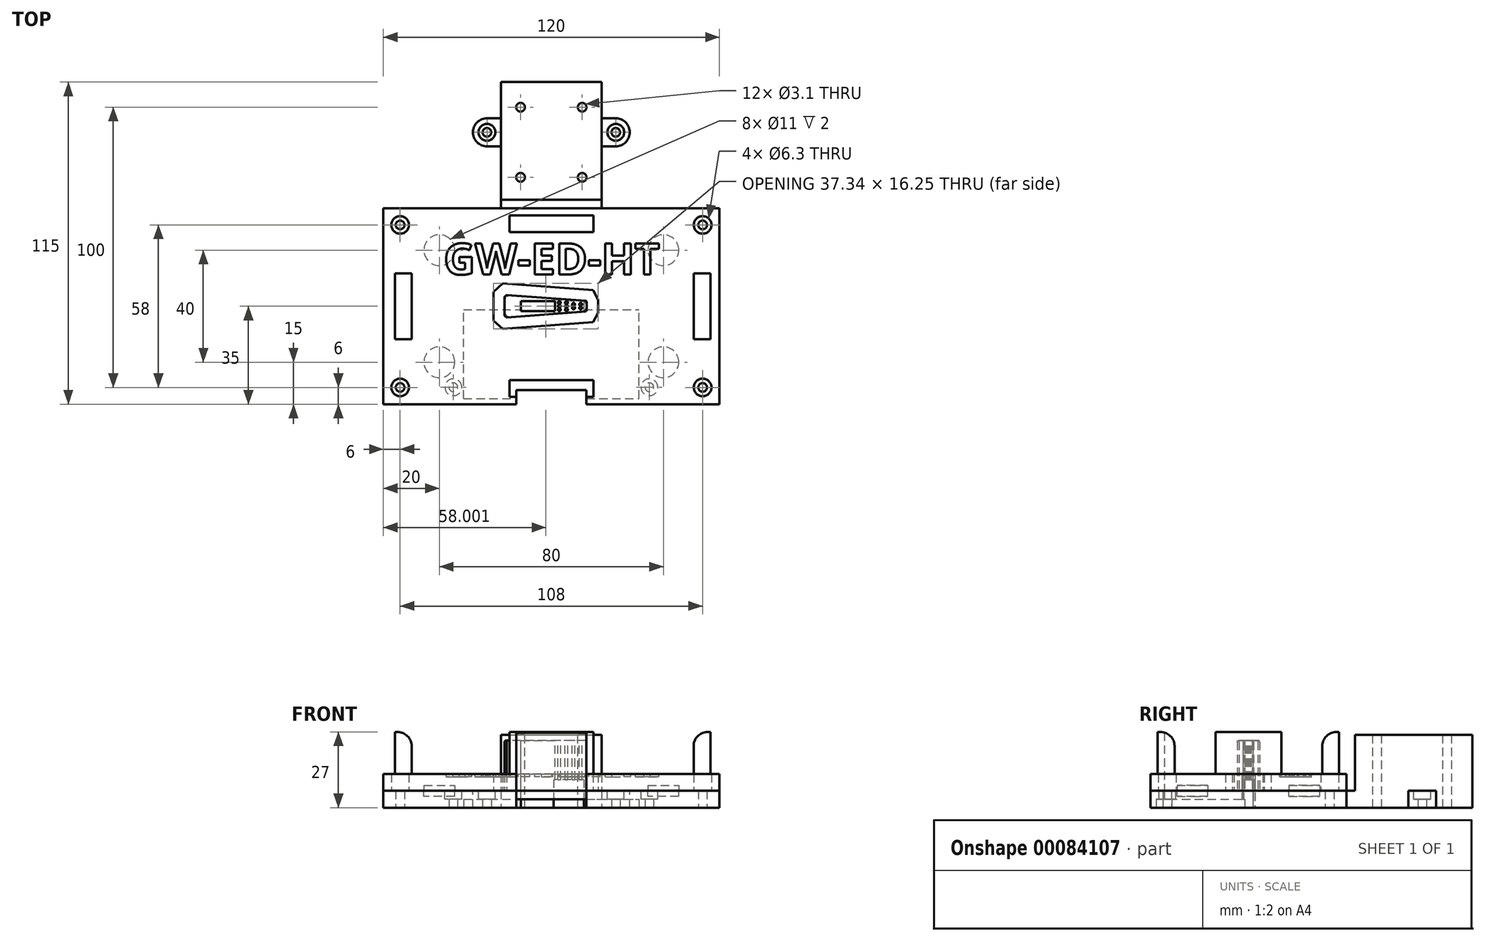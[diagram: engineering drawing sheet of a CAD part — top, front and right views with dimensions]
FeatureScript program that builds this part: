
annotation { "Feature Type Name" : "Feature", "Feature Type Description" : "" }
export const myFeature = defineFeature(function(context is Context, id is Id, definition is map)
    precondition{}
    {
        {
            var Q0;
            Q0=qCreatedBy(makeId("Top.planeOp"),FACE);
            var sketch = newSketch(context, id + "F0", { "sketchPlane" : qUnion([Q0])});
            skLineSegment(sketch, "E0.bottom", {"start": v(-60, 35) * mm, "end": v(60, 35) * mm});
            skLineSegment(sketch, "E0.top", {"start": v(-60, -35) * mm, "end": v(60, -35) * mm});
            skLineSegment(sketch, "E0.left", {"start": v(-60, 35) * mm, "end": v(-60, -35) * mm});
            skLineSegment(sketch, "E0.right", {"start": v(60, 35) * mm, "end": v(60, -35) * mm});
            skCircle(sketch, "E1", {"center": v(-54, 29) * mm, "radius": 1.55 * mm});
            skCircle(sketch, "E2", {"center": v(54, 29) * mm, "radius": 1.55 * mm});
            skCircle(sketch, "E3", {"center": v(54, -29) * mm, "radius": 1.55 * mm});
            skCircle(sketch, "E4", {"center": v(-54, -29) * mm, "radius": 1.55 * mm});
            skLineSegment(sketch, "E5.bottom", {"start": v(-18, 35) * mm, "end": v(18, 35) * mm});
            skLineSegment(sketch, "E5.top", {"start": v(-18, 80) * mm, "end": v(18, 80) * mm});
            skLineSegment(sketch, "E5.left", {"start": v(-18, 35) * mm, "end": v(-18, 80) * mm});
            skLineSegment(sketch, "E5.right", {"start": v(18, 35) * mm, "end": v(18, 80) * mm});
            skLineSegment(sketch, "E6.bottom", {"start": v(-18, 67.06) * mm, "end": v(-28, 67.06) * mm});
            skLineSegment(sketch, "E6.top", {"start": v(-18, 57.06) * mm, "end": v(-28, 57.06) * mm});
            skLineSegment(sketch, "E6.left", {"start": v(-18, 67.06) * mm, "end": v(-18, 57.06) * mm});
            skLineSegment(sketch, "E6.right", {"start": v(-28, 67.06) * mm, "end": v(-28, 57.06) * mm});
            skLineSegment(sketch, "E7.bottom", {"start": v(18, 67.06) * mm, "end": v(28, 67.06) * mm});
            skLineSegment(sketch, "E7.top", {"start": v(18, 57.06) * mm, "end": v(28, 57.06) * mm});
            skLineSegment(sketch, "E7.left", {"start": v(18, 67.06) * mm, "end": v(18, 57.06) * mm});
            skLineSegment(sketch, "E7.right", {"start": v(28, 67.06) * mm, "end": v(28, 57.06) * mm});
            skCircle(sketch, "E8", {"center": v(-23, 62.06) * mm, "radius": 1.55 * mm});
            skCircle(sketch, "E9", {"center": v(23, 62.06) * mm, "radius": 1.55 * mm});
            skCircle(sketch, "E10", {"center": v(-35, -28.94) * mm, "radius": 1.55 * mm});
            skCircle(sketch, "E11", {"center": v(35, -28.94) * mm, "radius": 1.55 * mm});
            skPoint(sketch, "E12", {"position": v(-28, 62.06) * mm});
            skSolve(sketch);
        }
        {
            var Q0;
            Q0 = qSketchRegion(id + "F0", true);
            extrude(context, id + "F1", {"entities" : qUnion([Q0]), "depth" : 6 * mm});
        }
        {
            var Q0;
            Q0=makeQuery(id+"F1.opExtrude","CAP_FACE",FACE,{"disambiguationData":[OSD([sQuery(id+"F0.wireOp",EDGE,"E0.bottom"),sQuery(id+"F0.wireOp",EDGE,"E0.top"),sQuery(id+"F0.wireOp",EDGE,"E0.left"),sQuery(id+"F0.wireOp",EDGE,"E0.right"),sQuery(id+"F0.wireOp",EDGE,"E1"),sQuery(id+"F0.wireOp",EDGE,"E2"),sQuery(id+"F0.wireOp",EDGE,"E3"),sQuery(id+"F0.wireOp",EDGE,"E4")])],"isStart":false});
            var sketch = newSketch(context, id + "F2", { "sketchPlane" : qUnion([Q0])});
            skLineSegment(sketch, "E13.0", {"start": v(12.67, -1.36) * mm, "end": v(12.67, 1.36) * mm});
            skLineSegment(sketch, "E13.1", {"start": v(12.4, -1.88) * mm, "end": v(12.67, -1.36) * mm});
            skLineSegment(sketch, "E13.2", {"start": v(12.67, 1.36) * mm, "end": v(12.4, 1.88) * mm});
            skLineSegment(sketch, "E13.3", {"start": v(-15.98, -4) * mm, "end": v(12.4, -1.88) * mm});
            skLineSegment(sketch, "E13.4", {"start": v(12.4, 1.88) * mm, "end": v(-15.98, 4) * mm});
            skLineSegment(sketch, "E13.5", {"start": v(-15.98, 4) * mm, "end": v(-16.67, 3.38) * mm});
            skLineSegment(sketch, "E13.6", {"start": v(-16.67, 3.38) * mm, "end": v(-16.67, -3.38) * mm});
            skLineSegment(sketch, "E13.7", {"start": v(-16.67, -3.38) * mm, "end": v(-15.98, -4) * mm});
            skSolve(sketch);
        }
        {
            var Q0;
            Q0 = qSketchRegion(id + "F2", true);
            extrude(context, id + "F3", {"entities" : qUnion([Q0]), "operationType" : NewBodyOperationType.ADD, "depth" : 18 * mm});
        }
        {
            var Q0;
            Q0=makeQuery(id+"F3.opExtrude","CAP_FACE",FACE,{"disambiguationData":[OSD([sQuery(id+"F2.wireOp",EDGE,"E13.0"),sQuery(id+"F2.wireOp",EDGE,"E13.1"),sQuery(id+"F2.wireOp",EDGE,"E13.2"),sQuery(id+"F2.wireOp",EDGE,"E13.3"),sQuery(id+"F2.wireOp",EDGE,"E13.4"),sQuery(id+"F2.wireOp",EDGE,"E13.5"),sQuery(id+"F2.wireOp",EDGE,"E13.6"),sQuery(id+"F2.wireOp",EDGE,"E13.7")])],"isStart":false});
            var sketch = newSketch(context, id + "F4", { "sketchPlane" : qUnion([Q0])});
            skCircle(sketch, "E14", {"center": v(10.47, 0.64) * mm, "radius": 0.5 * mm});
            skCircle(sketch, "E15", {"center": v(10.47, -0.64) * mm, "radius": 0.5 * mm});
            skCircle(sketch, "E16", {"center": v(7.93, 0.64) * mm, "radius": 0.5 * mm});
            skCircle(sketch, "E17", {"center": v(7.93, -0.64) * mm, "radius": 0.5 * mm});
            skCircle(sketch, "E18", {"center": v(5.4, 1.27) * mm, "radius": 0.5 * mm});
            skCircle(sketch, "E19", {"center": v(5.4, 0) * mm, "radius": 0.5 * mm});
            skCircle(sketch, "E20", {"center": v(5.4, -1.27) * mm, "radius": 0.5 * mm});
            skCircle(sketch, "E21", {"center": v(2.85, 1.27) * mm, "radius": 0.5 * mm});
            skCircle(sketch, "E22", {"center": v(2.85, 0) * mm, "radius": 0.5 * mm});
            skCircle(sketch, "E23", {"center": v(2.85, -1.27) * mm, "radius": 0.5 * mm});
            skLineSegment(sketch, "E24.bottom", {"start": v(-10.87, 1.78) * mm, "end": v(1.35, 1.78) * mm});
            skLineSegment(sketch, "E24.top", {"start": v(-10.87, -1.78) * mm, "end": v(1.35, -1.78) * mm});
            skLineSegment(sketch, "E24.left", {"start": v(-10.87, 1.78) * mm, "end": v(-10.87, -1.78) * mm});
            skLineSegment(sketch, "E24.right", {"start": v(1.35, 1.78) * mm, "end": v(1.35, -1.78) * mm});
            skSolve(sketch);
        }
        {
            var Q0;
            Q0 = qSketchRegion(id + "F4", true);
            extrude(context, id + "F5", {"entities" : qUnion([Q0]), "operationType" : NewBodyOperationType.REMOVE, "endBound" : BoundingType.THROUGH_ALL, "oppositeDirection" : true, "depth" : 25 * mm});
        }
        {
            var Q0;
            Q0=makeQuery(id+"F1.opExtrude","CAP_FACE",FACE,{"disambiguationData":[OSD([sQuery(id+"F0.wireOp",EDGE,"E0.bottom"),sQuery(id+"F0.wireOp",EDGE,"E0.top"),sQuery(id+"F0.wireOp",EDGE,"E0.left"),sQuery(id+"F0.wireOp",EDGE,"E0.right"),sQuery(id+"F0.wireOp",EDGE,"E1"),sQuery(id+"F0.wireOp",EDGE,"E2"),sQuery(id+"F0.wireOp",EDGE,"E3"),sQuery(id+"F0.wireOp",EDGE,"E4")])],"isStart":true});
            var sketch = newSketch(context, id + "F6", { "sketchPlane" : qUnion([Q0])});
            skLineSegment(sketch, "E25", {"start": v(0.79, 2.33) * mm, "end": v(0.79, -2.33) * mm});
            skLineSegment(sketch, "E26", {"start": v(0.79, -2.33) * mm, "end": v(11.64, -1.64) * mm});
            skLineSegment(sketch, "E27", {"start": v(11.64, -1.64) * mm, "end": v(11.64, 1.64) * mm});
            skLineSegment(sketch, "E28", {"start": v(11.64, 1.64) * mm, "end": v(0.79, 2.33) * mm});
            skSolve(sketch);
        }
        {
            var Q0;
            Q0 = qSketchRegion(id + "F6", true);
            extrude(context, id + "F7", {"entities" : qUnion([Q0]), "operationType" : NewBodyOperationType.REMOVE, "oppositeDirection" : true, "depth" : 10 * mm});
        }
        {
            var Q0;
            Q0=makeQuery(id+"F1.opExtrude","CAP_FACE",FACE,{"disambiguationData":[OSD([sQuery(id+"F0.wireOp",EDGE,"E0.bottom"),sQuery(id+"F0.wireOp",EDGE,"E0.top"),sQuery(id+"F0.wireOp",EDGE,"E0.left"),sQuery(id+"F0.wireOp",EDGE,"E0.right"),sQuery(id+"F0.wireOp",EDGE,"E1"),sQuery(id+"F0.wireOp",EDGE,"E2"),sQuery(id+"F0.wireOp",EDGE,"E3"),sQuery(id+"F0.wireOp",EDGE,"E4")])],"isStart":false});
            var sketch = newSketch(context, id + "F8", { "sketchPlane" : qUnion([Q0])});
            skLineSegment(sketch, "E29.bottom", {"start": v(-60, 35) * mm, "end": v(60, 35) * mm});
            skLineSegment(sketch, "E29.top", {"start": v(-60, -35) * mm, "end": v(60, -35) * mm});
            skLineSegment(sketch, "E29.left", {"start": v(-60, 35) * mm, "end": v(-60, -35) * mm});
            skLineSegment(sketch, "E29.right", {"start": v(60, 35) * mm, "end": v(60, -35) * mm});
            skCircle(sketch, "E30", {"center": v(-54, 29) * mm, "radius": 3.15 * mm});
            skCircle(sketch, "E31", {"center": v(54, 29) * mm, "radius": 3.15 * mm});
            skCircle(sketch, "E32", {"center": v(54, -29) * mm, "radius": 3.15 * mm});
            skCircle(sketch, "E33", {"center": v(-54, -29) * mm, "radius": 3.15 * mm});
            skLineSegment(sketch, "E34.0", {"start": v(-20.67, -5.14) * mm, "end": v(-17.4, -8.13) * mm});
            skLineSegment(sketch, "E34.1", {"start": v(-20.67, 5.14) * mm, "end": v(-20.67, -5.14) * mm});
            skLineSegment(sketch, "E34.2", {"start": v(-17.4, -8.13) * mm, "end": v(14.9, -5.7) * mm});
            skLineSegment(sketch, "E34.3", {"start": v(-17.4, 8.13) * mm, "end": v(-20.67, 5.14) * mm});
            skLineSegment(sketch, "E34.4", {"start": v(14.9, -5.7) * mm, "end": v(16.67, -2.35) * mm});
            skLineSegment(sketch, "E34.5", {"start": v(16.67, -2.35) * mm, "end": v(16.67, 2.35) * mm});
            skLineSegment(sketch, "E34.6", {"start": v(16.67, 2.35) * mm, "end": v(14.9, 5.7) * mm});
            skLineSegment(sketch, "E34.7", {"start": v(14.9, 5.7) * mm, "end": v(-17.4, 8.13) * mm});
            skSolve(sketch);
        }
        {
            var Q0;
            Q0 = qSketchRegion(id + "F8", true);
            extrude(context, id + "F9", {"entities" : qUnion([Q0]), "depth" : 6 * mm});
        }
        {
            var Q0;
            Q0=makeQuery(id+"F9.opExtrude","CAP_FACE",FACE,{"disambiguationData":[OSD([sQuery(id+"F8.wireOp",EDGE,"E29.bottom"),sQuery(id+"F8.wireOp",EDGE,"E29.top"),sQuery(id+"F8.wireOp",EDGE,"E29.left"),sQuery(id+"F8.wireOp",EDGE,"E29.right"),sQuery(id+"F8.wireOp",EDGE,"E30"),sQuery(id+"F8.wireOp",EDGE,"E31"),sQuery(id+"F8.wireOp",EDGE,"E32"),sQuery(id+"F8.wireOp",EDGE,"E33"),sQuery(id+"F8.wireOp",EDGE,"E34.0"),sQuery(id+"F8.wireOp",EDGE,"E34.1"),sQuery(id+"F8.wireOp",EDGE,"E34.2"),sQuery(id+"F8.wireOp",EDGE,"E34.3"),sQuery(id+"F8.wireOp",EDGE,"E34.4"),sQuery(id+"F8.wireOp",EDGE,"E34.5"),sQuery(id+"F8.wireOp",EDGE,"E34.6"),sQuery(id+"F8.wireOp",EDGE,"E34.7")])],"isStart":false});
            var sketch = newSketch(context, id + "F10", { "sketchPlane" : qUnion([Q0])});
            skLineSegment(sketch, "E35.bottom", {"start": v(-55.9, 11.73) * mm, "end": v(-49.9, 11.73) * mm});
            skLineSegment(sketch, "E35.top", {"start": v(-55.9, -11.73) * mm, "end": v(-49.9, -11.73) * mm});
            skLineSegment(sketch, "E35.left", {"start": v(-55.9, 11.73) * mm, "end": v(-55.9, -11.73) * mm});
            skLineSegment(sketch, "E35.right", {"start": v(-49.9, 11.73) * mm, "end": v(-49.9, -11.73) * mm});
            skLineSegment(sketch, "E36.bottom", {"start": v(-15, 32.38) * mm, "end": v(15, 32.38) * mm});
            skLineSegment(sketch, "E36.top", {"start": v(-15, 26.38) * mm, "end": v(15, 26.37) * mm});
            skLineSegment(sketch, "E36.left", {"start": v(-15, 32.37) * mm, "end": v(-15, 26.37) * mm});
            skLineSegment(sketch, "E36.right", {"start": v(15, 32.37) * mm, "end": v(15, 26.37) * mm});
            skLineSegment(sketch, "E37.bottom", {"start": v(-15, -26.37) * mm, "end": v(15, -26.38) * mm});
            skLineSegment(sketch, "E37.top", {"start": v(-15, -32.37) * mm, "end": v(15, -32.37) * mm});
            skLineSegment(sketch, "E37.left", {"start": v(-15, -26.37) * mm, "end": v(-15, -32.37) * mm});
            skLineSegment(sketch, "E37.right", {"start": v(15, -26.37) * mm, "end": v(15, -32.37) * mm});
            skLineSegment(sketch, "E38.bottom", {"start": v(50.8, 11.73) * mm, "end": v(56.8, 11.73) * mm});
            skLineSegment(sketch, "E38.top", {"start": v(50.8, -11.73) * mm, "end": v(56.8, -11.73) * mm});
            skLineSegment(sketch, "E38.left", {"start": v(50.8, 11.73) * mm, "end": v(50.8, -11.73) * mm});
            skLineSegment(sketch, "E38.right", {"start": v(56.8, 11.73) * mm, "end": v(56.8, -11.73) * mm});
            skSolve(sketch);
        }
        {
            var Q0;
            Q0 = qSketchRegion(id + "F10", true);
            extrude(context, id + "F11", {"entities" : qUnion([Q0]), "operationType" : NewBodyOperationType.ADD, "depth" : 15 * mm});
        }
        {
            var Q0;
            Q0=makeQuery(id+"F11.opExtrude","CAP_EDGE",EDGE,{"disambiguationData":[OSD([sQuery(id+"F10.wireOp",EDGE,"E37.bottom")])],"isStart":false});
            var Q1;
            Q1=makeQuery(id+"F11.opExtrude","CAP_EDGE",EDGE,{"disambiguationData":[OSD([sQuery(id+"F10.wireOp",EDGE,"E35.right")])],"isStart":false});
            var Q2;
            Q2=makeQuery(id+"F11.opExtrude","CAP_EDGE",EDGE,{"disambiguationData":[OSD([sQuery(id+"F10.wireOp",EDGE,"E36.top")])],"isStart":false});
            var Q3;
            Q3=makeQuery(id+"F11.opExtrude","CAP_EDGE",EDGE,{"disambiguationData":[OSD([sQuery(id+"F10.wireOp",EDGE,"E38.left")])],"isStart":false});
            fillet(context, id + "F12", {"entities" : qUnion([Q0, Q1, Q2, Q3]), "radius" : 5 * mm, "tangentPropagation" : true, "allowEdgeOverflow" : false});
        }
        {
            var Q0;
            Q0=makeQuery(id+"F3.opExtrude","CAP_EDGE",EDGE,{"disambiguationData":[OSD([sQuery(id+"F2.wireOp",EDGE,"E13.3")])],"isStart":false});
            var Q1;
            Q1=makeQuery(id+"F3.opExtrude","CAP_EDGE",EDGE,{"disambiguationData":[OSD([sQuery(id+"F2.wireOp",EDGE,"E13.4")])],"isStart":false});
            var Q2;
            Q2=makeQuery(id+"F3.opExtrude","CAP_EDGE",EDGE,{"disambiguationData":[OSD([sQuery(id+"F2.wireOp",EDGE,"E13.0")])],"isStart":false});
            var Q3;
            Q3=makeQuery(id+"F3.opExtrude","CAP_EDGE",EDGE,{"disambiguationData":[OSD([sQuery(id+"F2.wireOp",EDGE,"E13.2")])],"isStart":false});
            var Q4;
            Q4=makeQuery(id+"F3.opExtrude","CAP_EDGE",EDGE,{"disambiguationData":[OSD([sQuery(id+"F2.wireOp",EDGE,"E13.1")])],"isStart":false});
            var Q5;
            Q5=makeQuery(id+"F3.opExtrude","CAP_EDGE",EDGE,{"disambiguationData":[OSD([sQuery(id+"F2.wireOp",EDGE,"E13.7")])],"isStart":false});
            var Q6;
            Q6=makeQuery(id+"F3.opExtrude","CAP_EDGE",EDGE,{"disambiguationData":[OSD([sQuery(id+"F2.wireOp",EDGE,"E13.6")])],"isStart":false});
            var Q7;
            Q7=makeQuery(id+"F3.opExtrude","CAP_EDGE",EDGE,{"disambiguationData":[OSD([sQuery(id+"F2.wireOp",EDGE,"E13.5")])],"isStart":false});
            fillet(context, id + "F13", {"entities" : qUnion([Q0, Q1, Q2, Q3, Q4, Q5, Q6, Q7]), "radius" : 0.5 * mm, "tangentPropagation" : true, "allowEdgeOverflow" : false});
        }
        {
            var Q0;
            Q0=makeQuery(id+"F1.opExtrude","CAP_FACE",FACE,{"disambiguationData":[OSD([sQuery(id+"F0.wireOp",EDGE,"E0.bottom"),sQuery(id+"F0.wireOp",EDGE,"E0.top"),sQuery(id+"F0.wireOp",EDGE,"E0.left"),sQuery(id+"F0.wireOp",EDGE,"E0.right"),sQuery(id+"F0.wireOp",EDGE,"E1"),sQuery(id+"F0.wireOp",EDGE,"E2"),sQuery(id+"F0.wireOp",EDGE,"E3"),sQuery(id+"F0.wireOp",EDGE,"E4")])],"isStart":true});
            var sketch = newSketch(context, id + "F14", { "sketchPlane" : qUnion([Q0])});
            skLineSegment(sketch, "E39.bottom", {"start": v(-12.5, 35) * mm, "end": v(12.5, 35) * mm});
            skLineSegment(sketch, "E39.top", {"start": v(-12.5, 30) * mm, "end": v(12.5, 30) * mm});
            skLineSegment(sketch, "E39.left", {"start": v(-12.5, 35) * mm, "end": v(-12.5, 30) * mm});
            skLineSegment(sketch, "E39.right", {"start": v(12.5, 35) * mm, "end": v(12.5, 30) * mm});
            skSolve(sketch);
        }
        {
            var Q0;
            Q0 = qSketchRegion(id + "F14", true);
            extrude(context, id + "F15", {"entities" : qUnion([Q0]), "operationType" : NewBodyOperationType.REMOVE, "endBound" : BoundingType.THROUGH_ALL, "oppositeDirection" : true, "depth" : 25 * mm});
        }
        {
            var Q0;
            Q0=makeQuery(id+"F1.opExtrude","CAP_FACE",FACE,{"disambiguationData":[OSD([sQuery(id+"F0.wireOp",EDGE,"E0.bottom"),sQuery(id+"F0.wireOp",EDGE,"E0.top"),sQuery(id+"F0.wireOp",EDGE,"E0.left"),sQuery(id+"F0.wireOp",EDGE,"E0.right"),sQuery(id+"F0.wireOp",EDGE,"E1"),sQuery(id+"F0.wireOp",EDGE,"E2"),sQuery(id+"F0.wireOp",EDGE,"E3"),sQuery(id+"F0.wireOp",EDGE,"E4")])],"isStart":true});
            var sketch = newSketch(context, id + "F16", { "sketchPlane" : qUnion([Q0])});
            skLineSegment(sketch, "E40.bottom", {"start": v(-31.34, 33) * mm, "end": v(31.34, 33) * mm});
            skLineSegment(sketch, "E40.top", {"start": v(-31.34, 1.26) * mm, "end": v(31.34, 1.26) * mm});
            skLineSegment(sketch, "E40.left", {"start": v(-31.34, 33) * mm, "end": v(-31.34, 1.26) * mm});
            skLineSegment(sketch, "E40.right", {"start": v(31.34, 33) * mm, "end": v(31.34, 1.26) * mm});
            skSolve(sketch);
        }
        {
            var Q0;
            Q0 = qSketchRegion(id + "F16", true);
            extrude(context, id + "F17", {"entities" : qUnion([Q0]), "operationType" : NewBodyOperationType.REMOVE, "oppositeDirection" : true, "depth" : 3 * mm});
        }
        {
            var Q0;
            Q0=makeQuery(id+"F1.opExtrude","CAP_FACE",FACE,{"disambiguationData":[OSD([sQuery(id+"F0.wireOp",EDGE,"E0.bottom"),sQuery(id+"F0.wireOp",EDGE,"E0.top"),sQuery(id+"F0.wireOp",EDGE,"E0.left"),sQuery(id+"F0.wireOp",EDGE,"E0.right"),sQuery(id+"F0.wireOp",EDGE,"E1"),sQuery(id+"F0.wireOp",EDGE,"E2"),sQuery(id+"F0.wireOp",EDGE,"E3"),sQuery(id+"F0.wireOp",EDGE,"E4")])],"isStart":false});
            var sketch = newSketch(context, id + "F18", { "sketchPlane" : qUnion([Q0])});
            skCircle(sketch, "E41", {"center": v(-40, 20) * mm, "radius": 5.5 * mm});
            skCircle(sketch, "E42", {"center": v(-40, -20) * mm, "radius": 5.5 * mm});
            skCircle(sketch, "E43", {"center": v(40, -20) * mm, "radius": 5.5 * mm});
            skCircle(sketch, "E44", {"center": v(40, 20) * mm, "radius": 5.5 * mm});
            skSolve(sketch);
        }
        {
            var Q0;
            Q0 = qSketchRegion(id + "F18", true);
            extrude(context, id + "F19", {"entities" : qUnion([Q0]), "operationType" : NewBodyOperationType.REMOVE, "oppositeDirection" : true, "depth" : 2 * mm});
        }
        {
            var Q0;
            Q0=makeQuery(id+"F9.opExtrude","CAP_FACE",FACE,{"disambiguationData":[OSD([sQuery(id+"F8.wireOp",EDGE,"E29.bottom"),sQuery(id+"F8.wireOp",EDGE,"E29.top"),sQuery(id+"F8.wireOp",EDGE,"E29.left"),sQuery(id+"F8.wireOp",EDGE,"E29.right"),sQuery(id+"F8.wireOp",EDGE,"E30"),sQuery(id+"F8.wireOp",EDGE,"E31"),sQuery(id+"F8.wireOp",EDGE,"E32"),sQuery(id+"F8.wireOp",EDGE,"E33"),sQuery(id+"F8.wireOp",EDGE,"E34.0"),sQuery(id+"F8.wireOp",EDGE,"E34.1"),sQuery(id+"F8.wireOp",EDGE,"E34.2"),sQuery(id+"F8.wireOp",EDGE,"E34.3"),sQuery(id+"F8.wireOp",EDGE,"E34.4"),sQuery(id+"F8.wireOp",EDGE,"E34.5"),sQuery(id+"F8.wireOp",EDGE,"E34.6"),sQuery(id+"F8.wireOp",EDGE,"E34.7")])],"isStart":true});
            var sketch = newSketch(context, id + "F20", { "sketchPlane" : qUnion([Q0])});
            skCircle(sketch, "E45", {"center": v(-40, 20) * mm, "radius": 5.5 * mm});
            skCircle(sketch, "E46", {"center": v(-40, -20) * mm, "radius": 5.5 * mm});
            skCircle(sketch, "E47", {"center": v(40, -20) * mm, "radius": 5.5 * mm});
            skCircle(sketch, "E48", {"center": v(40, 20) * mm, "radius": 5.5 * mm});
            skSolve(sketch);
        }
        {
            var Q0;
            Q0 = qSketchRegion(id + "F20", true);
            extrude(context, id + "F21", {"entities" : qUnion([Q0]), "operationType" : NewBodyOperationType.REMOVE, "oppositeDirection" : true, "depth" : 2 * mm});
        }
        {
            var Q0;
            Q0=makeQuery(id+"F9.opExtrude","CAP_FACE",FACE,{"disambiguationData":[OSD([sQuery(id+"F8.wireOp",EDGE,"E29.bottom"),sQuery(id+"F8.wireOp",EDGE,"E29.top"),sQuery(id+"F8.wireOp",EDGE,"E29.left"),sQuery(id+"F8.wireOp",EDGE,"E29.right"),sQuery(id+"F8.wireOp",EDGE,"E30"),sQuery(id+"F8.wireOp",EDGE,"E31"),sQuery(id+"F8.wireOp",EDGE,"E32"),sQuery(id+"F8.wireOp",EDGE,"E33"),sQuery(id+"F8.wireOp",EDGE,"E34.0"),sQuery(id+"F8.wireOp",EDGE,"E34.1"),sQuery(id+"F8.wireOp",EDGE,"E34.2"),sQuery(id+"F8.wireOp",EDGE,"E34.3"),sQuery(id+"F8.wireOp",EDGE,"E34.4"),sQuery(id+"F8.wireOp",EDGE,"E34.5"),sQuery(id+"F8.wireOp",EDGE,"E34.6"),sQuery(id+"F8.wireOp",EDGE,"E34.7")])],"isStart":false});
            var sketch = newSketch(context, id + "F22", { "sketchPlane" : qUnion([Q0])});
            skText(sketch, "E49", { "text": "GW-ED-HT", "fontName": "OpenSans-Bold.ttf"});
            const initialGuessF22  = {"E49": [-0.03845, 0.0113, 1, 0, 0.01116]};
            skSetInitialGuess(sketch, initialGuessF22);
            skSolve(sketch);
        }
        {
            var Q0;
            Q0 = qSketchRegion(id + "F22", true);
            extrude(context, id + "F23", {"entities" : qUnion([Q0]), "operationType" : NewBodyOperationType.REMOVE, "oppositeDirection" : true, "depth" : 1 * mm});
        }
        {
            var Q0;
            Q0=makeQuery(id+"F1.opExtrude","CAP_FACE",FACE,{"disambiguationData":[OSD([sQuery(id+"F0.wireOp",EDGE,"E0.bottom"),sQuery(id+"F0.wireOp",EDGE,"E0.top"),sQuery(id+"F0.wireOp",EDGE,"E0.left"),sQuery(id+"F0.wireOp",EDGE,"E0.right"),sQuery(id+"F0.wireOp",EDGE,"E1"),sQuery(id+"F0.wireOp",EDGE,"E2"),sQuery(id+"F0.wireOp",EDGE,"E3"),sQuery(id+"F0.wireOp",EDGE,"E4"),sQuery(id+"F0.wireOp",EDGE,"E5.top"),sQuery(id+"F0.wireOp",EDGE,"E5.left"),sQuery(id+"F0.wireOp",EDGE,"E5.right")])],"isStart":false});
            var sketch = newSketch(context, id + "F24", { "sketchPlane" : qUnion([Q0])});
            skLineSegment(sketch, "E50.bottom", {"start": v(-18, 80) * mm, "end": v(18, 80) * mm});
            skLineSegment(sketch, "E50.top", {"start": v(-18, 38) * mm, "end": v(18, 38) * mm});
            skLineSegment(sketch, "E50.left", {"start": v(-18, 80) * mm, "end": v(-18, 38) * mm});
            skLineSegment(sketch, "E50.right", {"start": v(18, 80) * mm, "end": v(18, 38) * mm});
            skSolve(sketch);
        }
        {
            var Q0;
            Q0 = qSketchRegion(id + "F24", true);
            extrude(context, id + "F25", {"entities" : qUnion([Q0]), "operationType" : NewBodyOperationType.ADD, "depth" : 20 * mm});
        }
        {
            var Q0;
            Q0=makeQuery(id+"F25.opExtrude","CAP_FACE",FACE,{"disambiguationData":[OSD([sQuery(id+"F24.wireOp",EDGE,"E50.bottom"),sQuery(id+"F24.wireOp",EDGE,"E50.top"),sQuery(id+"F24.wireOp",EDGE,"E50.left"),sQuery(id+"F24.wireOp",EDGE,"E50.right")])],"isStart":false});
            var sketch = newSketch(context, id + "F26", { "sketchPlane" : qUnion([Q0])});
            skCircle(sketch, "E51", {"center": v(-11, 71) * mm, "radius": 1.55 * mm});
            skCircle(sketch, "E52", {"center": v(11, 71) * mm, "radius": 1.55 * mm});
            skCircle(sketch, "E53", {"center": v(-11, 46) * mm, "radius": 1.55 * mm});
            skCircle(sketch, "E54", {"center": v(11, 46) * mm, "radius": 1.55 * mm});
            skSolve(sketch);
        }
        {
            var Q0;
            Q0 = qSketchRegion(id + "F26", true);
            extrude(context, id + "F27", {"entities" : qUnion([Q0]), "operationType" : NewBodyOperationType.REMOVE, "endBound" : BoundingType.THROUGH_ALL, "oppositeDirection" : true, "depth" : 25 * mm});
        }
        {
            var Q0;
            {var subQ0=sQuery(id+"F0.wireOp",EDGE,"E0.left");var subQ1=sQuery(id+"F0.wireOp",EDGE,"E0.bottom");var subQ2=sQuery(id+"F0.wireOp",EDGE,"E5.left");var subQ5=sQuery(id+"F0.wireOp",EDGE,"E11");var subQ6=sQuery(id+"F0.wireOp",EDGE,"E0.right");var subQ7=sQuery(id+"F0.wireOp",EDGE,"E5.right");var subQ9=sQuery(id+"F0.wireOp",EDGE,"E5.top");var subQ11=sQuery(id+"F0.wireOp",EDGE,"E7.bottom");var subQ12=sQuery(id+"F0.wireOp",EDGE,"E7.top");var subQ14=sQuery(id+"F0.wireOp",EDGE,"E6.bottom");var subQ15=sQuery(id+"F0.wireOp",EDGE,"E6.top");var subQ16=sQuery(id+"F0.wireOp",EDGE,"E0.top");var subQ17=sQuery(id+"F0.wireOp",EDGE,"E4");var subQ18=sQuery(id+"F0.wireOp",EDGE,"E1");var subQ19=sQuery(id+"F0.wireOp",EDGE,"E10");var subQ20=sQuery(id+"F0.wireOp",EDGE,"E2");var subQ21=sQuery(id+"F0.wireOp",EDGE,"E3");Q0=makeQuery(id+"F25.boolean.opBoolean","SPLIT",FACE,{"disambiguationData":[TD([makeQuery(id+"F1.opExtrude","SWEPT_FACE",FACE,{"disambiguationData":[OSD([subQ16])]})])],"derivedFrom":makeQuery(id+"F1.opExtrude","CAP_FACE",FACE,{"disambiguationData":[OSD([subQ1,subQ16,subQ0,subQ6,subQ18,subQ20,subQ21,subQ17,subQ9,subQ2,subQ7,subQ14,subQ15,sQuery(id+"F0.wireOp",EDGE,"E6.right"),subQ11,subQ12,sQuery(id+"F0.wireOp",EDGE,"E7.right"),sQuery(id+"F0.wireOp",EDGE,"E8"),sQuery(id+"F0.wireOp",EDGE,"E9"),subQ19,subQ5])],"isStart":false})});}
            var sketch = newSketch(context, id + "F28", { "sketchPlane" : qUnion([Q0])});
            skCircle(sketch, "E55", {"center": v(-35, -28.94) * mm, "radius": 3 * mm});
            skCircle(sketch, "E56", {"center": v(35, -28.94) * mm, "radius": 3 * mm});
            skCircle(sketch, "E57", {"center": v(23, 62.06) * mm, "radius": 3 * mm});
            skCircle(sketch, "E58", {"center": v(-23, 62.06) * mm, "radius": 3 * mm});
            skSolve(sketch);
        }
        {
            var Q0;
            Q0 = qSketchRegion(id + "F28", true);
            extrude(context, id + "F29", {"entities" : qUnion([Q0]), "operationType" : NewBodyOperationType.REMOVE, "oppositeDirection" : true, "depth" : 3 * mm});
        }
        {
            var Q0;
            Q0=makeQuery(id+"F1.opExtrude","SWEPT_EDGE",EDGE,{"disambiguationData":[OSD([sQuery(id+"F0.wireOp",EDGE,"E6.top"),sQuery(id+"F0.wireOp",EDGE,"E6.right")])]});
            var Q1;
            Q1=makeQuery(id+"F1.opExtrude","SWEPT_EDGE",EDGE,{"disambiguationData":[OSD([sQuery(id+"F0.wireOp",EDGE,"E6.bottom"),sQuery(id+"F0.wireOp",EDGE,"E6.right")])]});
            var Q2;
            Q2=makeQuery(id+"F1.opExtrude","SWEPT_EDGE",EDGE,{"disambiguationData":[OSD([sQuery(id+"F0.wireOp",EDGE,"E7.top"),sQuery(id+"F0.wireOp",EDGE,"E7.right")])]});
            var Q3;
            Q3=makeQuery(id+"F1.opExtrude","SWEPT_EDGE",EDGE,{"disambiguationData":[OSD([sQuery(id+"F0.wireOp",EDGE,"E7.bottom"),sQuery(id+"F0.wireOp",EDGE,"E7.right")])]});
            fillet(context, id + "F30", {"entities" : qUnion([Q0, Q1, Q2, Q3]), "radius" : 5 * mm, "tangentPropagation" : true, "allowEdgeOverflow" : false});
        }
        {
            var Q0;
            Q0=makeQuery(id+"F1.opExtrude","SWEPT_BODY",BODY,{"disambiguationData":[OSD([sQuery(id+"F0.wireOp",EDGE,"E0.bottom"),sQuery(id+"F0.wireOp",EDGE,"E0.top"),sQuery(id+"F0.wireOp",EDGE,"E0.left"),sQuery(id+"F0.wireOp",EDGE,"E0.right"),sQuery(id+"F0.wireOp",EDGE,"E1"),sQuery(id+"F0.wireOp",EDGE,"E2"),sQuery(id+"F0.wireOp",EDGE,"E3"),sQuery(id+"F0.wireOp",EDGE,"E4"),sQuery(id+"F0.wireOp",EDGE,"E5.top"),sQuery(id+"F0.wireOp",EDGE,"E5.left"),sQuery(id+"F0.wireOp",EDGE,"E5.right"),sQuery(id+"F0.wireOp",EDGE,"E6.bottom"),sQuery(id+"F0.wireOp",EDGE,"E6.top"),sQuery(id+"F0.wireOp",EDGE,"E6.right"),sQuery(id+"F0.wireOp",EDGE,"E7.bottom"),sQuery(id+"F0.wireOp",EDGE,"E7.top"),sQuery(id+"F0.wireOp",EDGE,"E7.right"),sQuery(id+"F0.wireOp",EDGE,"E8"),sQuery(id+"F0.wireOp",EDGE,"E9"),sQuery(id+"F0.wireOp",EDGE,"E10"),sQuery(id+"F0.wireOp",EDGE,"E11")])]});
            transform(context, id + "F31", {"entities" : qUnion([Q0]), "transformType" : TransformType.TRANSLATION_3D, "dx" : 0 * mm, "dy" : 0 * mm, "dz" : 0 * mm, "makeCopy" : true});
        }
        {
            var Q0;
            Q0=makeQuery(id+"F31.opPattern","COPY",BODY,{"derivedFrom":makeQuery(id+"F1.opExtrude","SWEPT_BODY",BODY,{"disambiguationData":[OSD([sQuery(id+"F0.wireOp",EDGE,"E0.bottom"),sQuery(id+"F0.wireOp",EDGE,"E0.top"),sQuery(id+"F0.wireOp",EDGE,"E0.left"),sQuery(id+"F0.wireOp",EDGE,"E0.right"),sQuery(id+"F0.wireOp",EDGE,"E1"),sQuery(id+"F0.wireOp",EDGE,"E2"),sQuery(id+"F0.wireOp",EDGE,"E3"),sQuery(id+"F0.wireOp",EDGE,"E4"),sQuery(id+"F0.wireOp",EDGE,"E5.top"),sQuery(id+"F0.wireOp",EDGE,"E5.left"),sQuery(id+"F0.wireOp",EDGE,"E5.right"),sQuery(id+"F0.wireOp",EDGE,"E6.bottom"),sQuery(id+"F0.wireOp",EDGE,"E6.top"),sQuery(id+"F0.wireOp",EDGE,"E6.right"),sQuery(id+"F0.wireOp",EDGE,"E7.bottom"),sQuery(id+"F0.wireOp",EDGE,"E7.top"),sQuery(id+"F0.wireOp",EDGE,"E7.right"),sQuery(id+"F0.wireOp",EDGE,"E8"),sQuery(id+"F0.wireOp",EDGE,"E9"),sQuery(id+"F0.wireOp",EDGE,"E10"),sQuery(id+"F0.wireOp",EDGE,"E11")])]}),"instanceName":"1"});
            deleteBodies(context, id + "F32", {"entities" : qUnion([Q0])});
        }
    });
